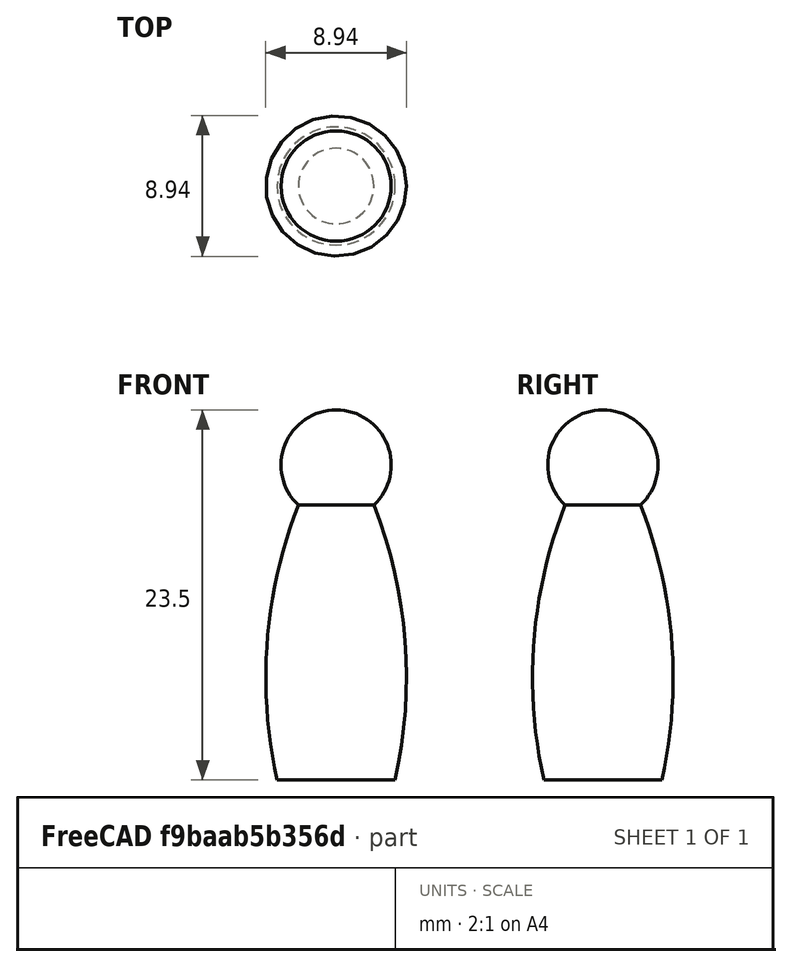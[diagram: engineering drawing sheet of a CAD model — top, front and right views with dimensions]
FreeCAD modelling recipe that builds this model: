
FCSTD DOCUMENT  (FreeCAD 0.16R)
Label: CatanRobber
License: All rights reserved
LicenseURL: http://en.wikipedia.org/wiki/All_rights_reserved
objects: Sketcher::SketchObject×1, PartDesign::Revolution×1, Mesh::Feature×1
note: 3 computed .brp shape members not serialized (recipe doc carries the construction recipe); baked Part::Feature solids carry a one-line shape summary decoded from their .brp

FEATURE [Sketcher::SketchObject] Sketch
  Placement = pos=(0,0,0) rot=(-1,0,0;4.71239rad)
  sketch-geometry (4):
    g0: ArcOfCircle CenterX=-25.5344 CenterY=6.5132 CenterZ=0 NormalX=0 NormalY=0 NormalZ=1 Radius=30 StartAngle=6.06434 EndAngle=6.65643
    g1: LineSegment StartX=0 StartY=0 StartZ=0 EndX=3.75 EndY=0 EndZ=0
    g2: ArcOfCircle CenterX=0 CenterY=20 CenterZ=0 NormalX=0 NormalY=0 NormalZ=1 Radius=3.5 StartAngle=5.46797 EndAngle=7.85398
    g3: LineSegment StartX=0 StartY=23.5 StartZ=0 EndX=0 EndY=0 EndZ=0
  constraints (14):
    c: PointOnObject(g0,g-1)
    c: Coincident(g1,g-1)
    c: Coincident(g1,g0)
    c: Radius(g0) = 30
    c: DistanceY(g2) = 20
    c: Radius(g2) = 3.5
    c: Coincident(g0,g2)
    c: Perpendicular(g2,g-2)
    c: DistanceX(g0) = 2.4
    c: DistanceX(g0) = 3.75
    c: PointOnObject(g2,g-2)
    c: Coincident(g3,g-1)
    c: Vertical(g3)
    c: Coincident(g3,g2)
FEATURE [PartDesign::Revolution] Revolution
  Angle = 360
  Axis = (0,0,1)
  Base = (0,0,0)
  Placement = pos=(0,0,0) rot=(-1,0,0;4.71239rad)
  ReferenceAxis = -> Sketch [V_Axis]
  Reversed = true
  Sketch = -> Sketch
FEATURE [Mesh::Feature] Mesh  label="Revolution (Meshed)"
